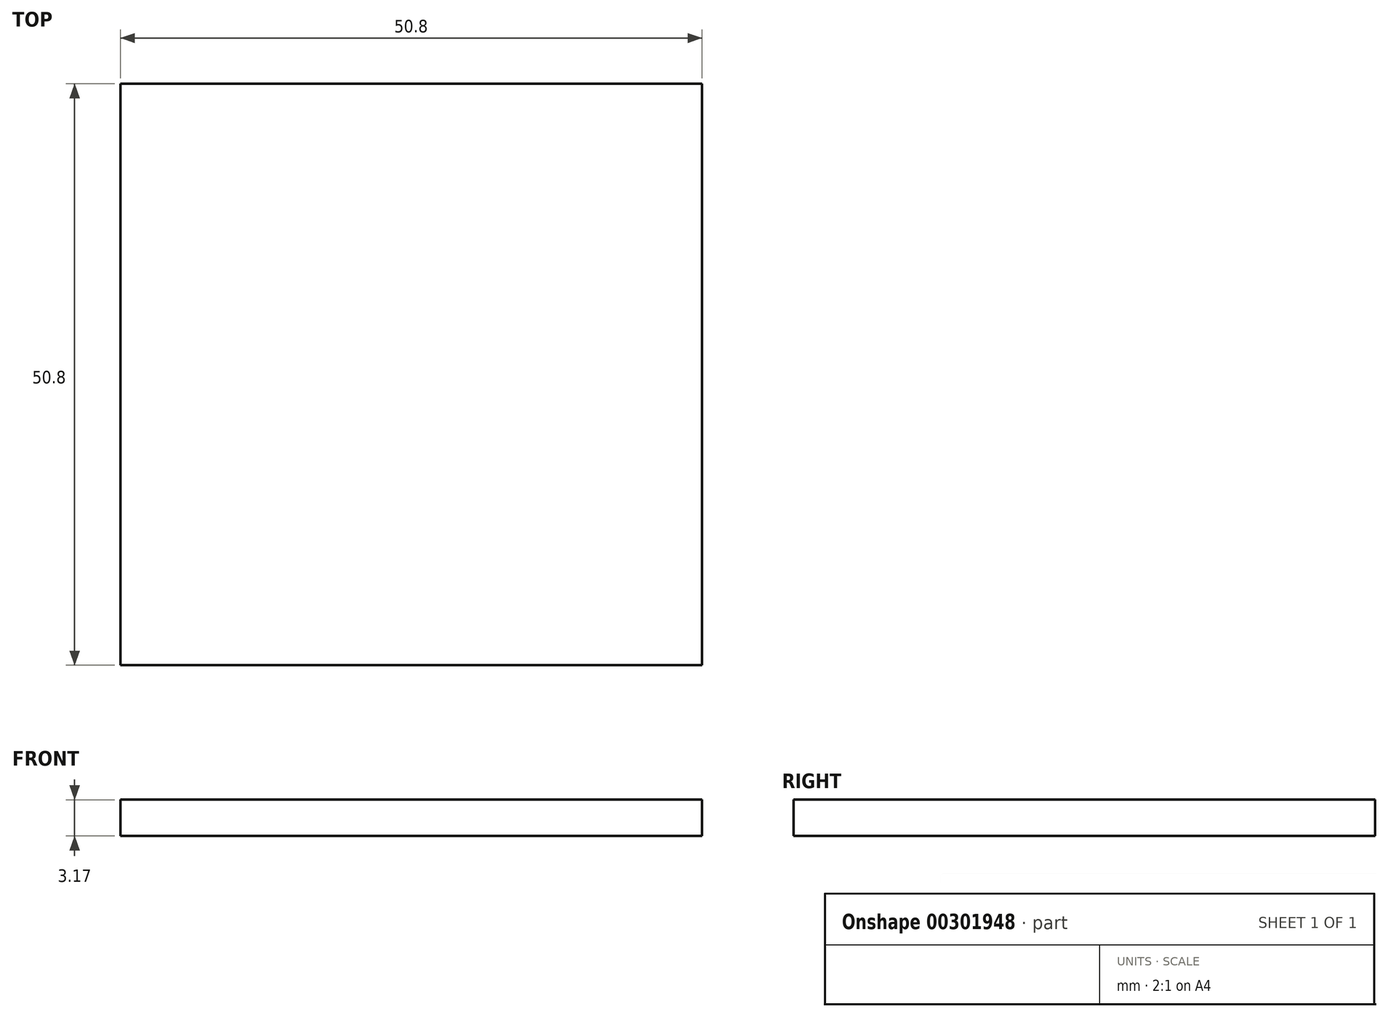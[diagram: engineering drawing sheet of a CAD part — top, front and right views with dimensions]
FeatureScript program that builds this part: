
annotation { "Feature Type Name" : "Feature", "Feature Type Description" : "" }
export const myFeature = defineFeature(function(context is Context, id is Id, definition is map)
    precondition{}
    {
        {
            var Q0;
            Q0=qCreatedBy(makeId("Top.planeOp"),FACE);
            var sketch = newSketch(context, id + "F0", { "sketchPlane" : qUnion([Q0])});
            skLineSegment(sketch, "E0.bottom", {"start": v(-25.4, 25.4) * mm, "end": v(25.4, 25.4) * mm});
            skLineSegment(sketch, "E0.top", {"start": v(-25.4, -25.4) * mm, "end": v(25.4, -25.4) * mm});
            skLineSegment(sketch, "E0.left", {"start": v(-25.4, 25.4) * mm, "end": v(-25.4, -25.4) * mm});
            skLineSegment(sketch, "E0.right", {"start": v(25.4, 25.4) * mm, "end": v(25.4, -25.4) * mm});
            skPoint(sketch, "E0.middle", {"position": v(0, 0) * mm});
            skSolve(sketch);
        }
        {
            var Q0;
            Q0 = qSketchRegion(id + "F0", true);
            extrude(context, id + "F1", {"entities" : qUnion([Q0]), "depth" : 3.17 * mm});
        }
    });
